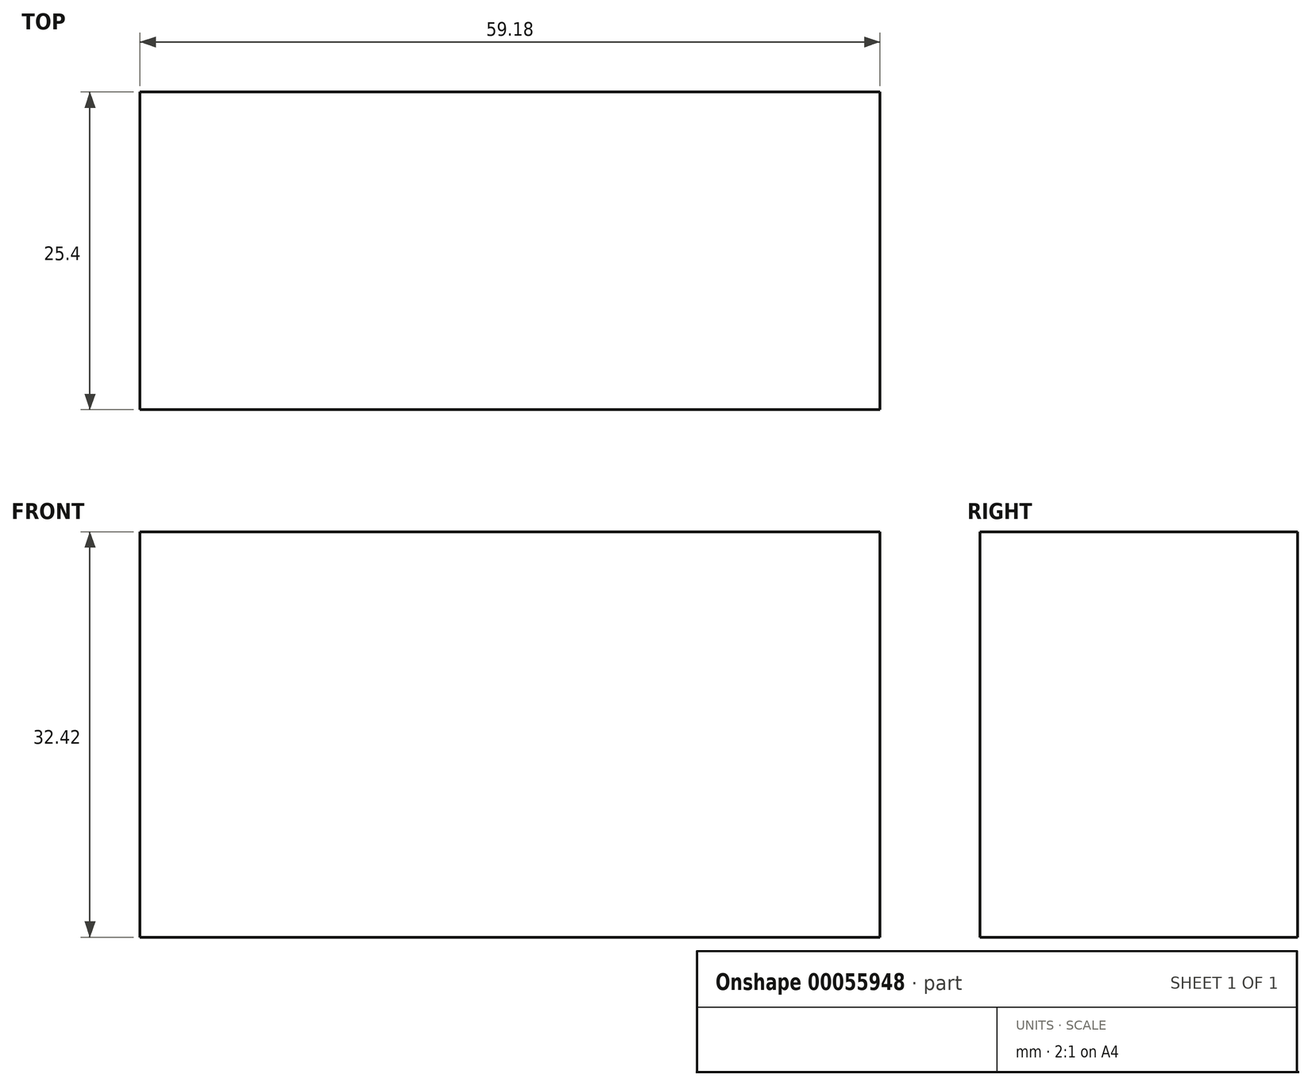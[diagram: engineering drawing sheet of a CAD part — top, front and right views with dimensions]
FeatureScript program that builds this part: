
annotation { "Feature Type Name" : "Feature", "Feature Type Description" : "" }
export const myFeature = defineFeature(function(context is Context, id is Id, definition is map)
    precondition{}
    {
        {
            var Q0;
            Q0=qCreatedBy(makeId("Front.planeOp"),FACE);
            var sketch = newSketch(context, id + "F0", { "sketchPlane" : qUnion([Q0])});
            skLineSegment(sketch, "E0.bottom", {"start": v(-65.21, 68.14) * mm, "end": v(-6.03, 68.14) * mm});
            skLineSegment(sketch, "E0.top", {"start": v(-65.21, 35.72) * mm, "end": v(-6.03, 35.72) * mm});
            skLineSegment(sketch, "E0.left", {"start": v(-65.21, 68.14) * mm, "end": v(-65.21, 35.72) * mm});
            skLineSegment(sketch, "E0.right", {"start": v(-6.03, 68.14) * mm, "end": v(-6.03, 35.72) * mm});
            skSolve(sketch);
        }
        {
            var Q0;
            Q0 = qSketchRegion(id + "F0", true);
            extrude(context, id + "F1", {"entities" : qUnion([Q0]), "depth" : 25.4 * mm});
        }
    });
